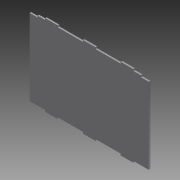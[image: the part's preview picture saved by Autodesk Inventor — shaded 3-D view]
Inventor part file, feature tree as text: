
AUTODESK INVENTOR PART (.ipt)
format: ipt  version: 2011 (Build 150239000, 239)  size: 106,496 bytes
history: native  units: in
note: dims shown in document units (in); Inventor stores cm internally (conversion verified against a paired STEP export)
features: extrude x1, sketch x1
ambient origin geometry x8: Origin, YZ Plane, XZ Plane, XY Plane, X Axis, Y Axis, Z Axis, Center Point
bodies: Solid1 (feature_tree)
feature tree (2):
  extrude  "Extrusion1"  Depth=12.35in
  sketch  "Sketch1"  dims[d0=18.9in d1=12.35in d2=10.45in d3=2.0in d4=0.25in d5=4.0in d6=10.0in d7=2.0in d8=2.0in d9=0.25in d10=1.26in d11=0.26in d12=1.26in d13=0.25in d14=0.0in]
